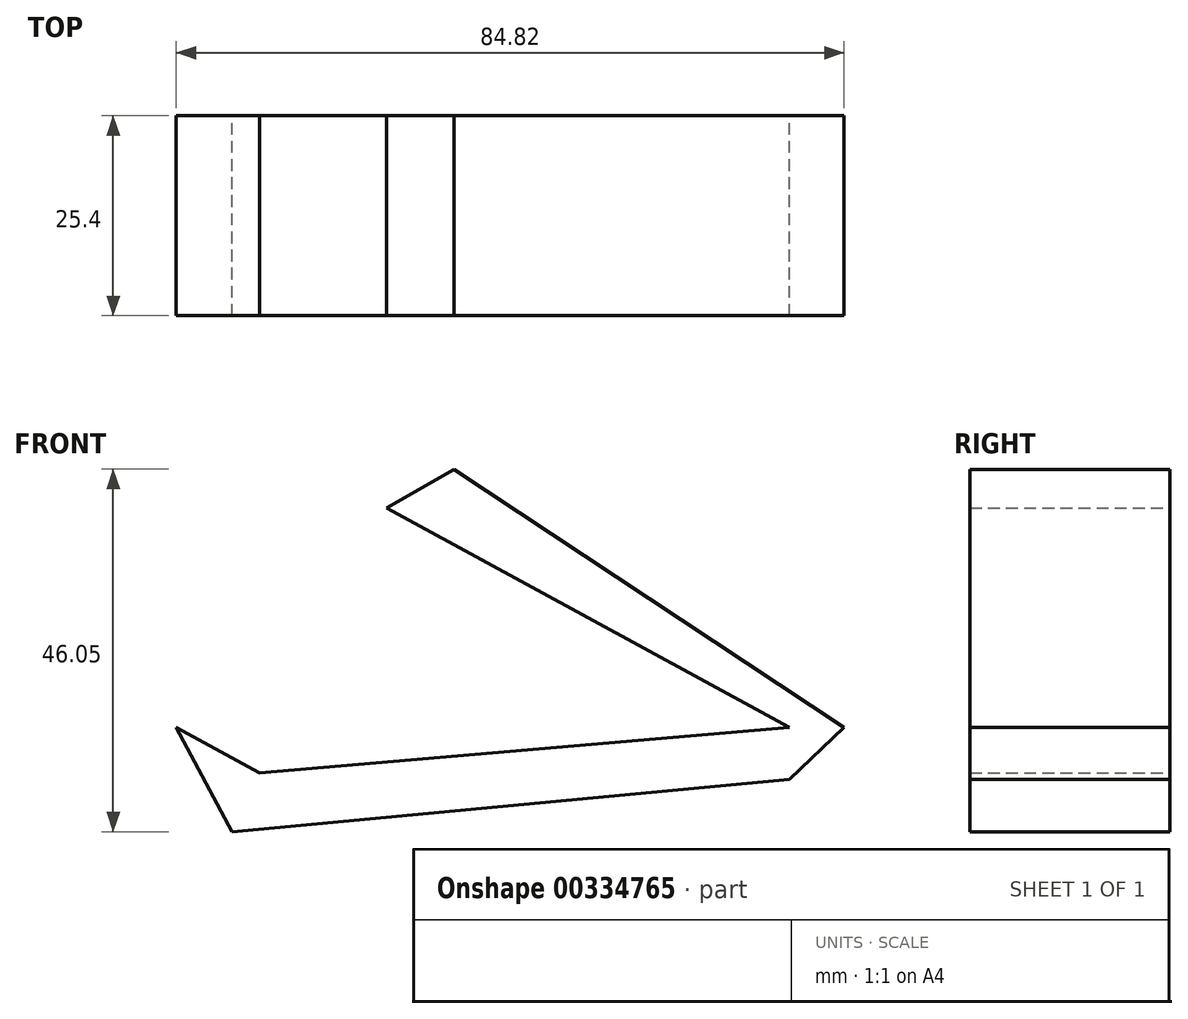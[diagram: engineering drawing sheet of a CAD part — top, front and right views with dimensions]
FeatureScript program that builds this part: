
annotation { "Feature Type Name" : "Feature", "Feature Type Description" : "" }
export const myFeature = defineFeature(function(context is Context, id is Id, definition is map)
    precondition{}
    {
        {
            var Q0;
            Q0=qCreatedBy(makeId("Front.planeOp"),FACE);
            var sketch = newSketch(context, id + "F0", { "sketchPlane" : qUnion([Q0])});
            skLineSegment(sketch, "E0", {"start": v(-51.23, 49.21) * mm, "end": v(0, 21.3) * mm});
            skLineSegment(sketch, "E1", {"start": v(0, 21.3) * mm, "end": v(-67.35, 15.54) * mm});
            skLineSegment(sketch, "E2", {"start": v(-67.35, 15.54) * mm, "end": v(-77.9, 21.3) * mm});
            skLineSegment(sketch, "E3", {"start": v(-77.9, 21.3) * mm, "end": v(-70.8, 8.06) * mm});
            skLineSegment(sketch, "E4", {"start": v(-70.8, 8.06) * mm, "end": v(0, 14.68) * mm});
            skLineSegment(sketch, "E5", {"start": v(0, 14.68) * mm, "end": v(6.9, 21.3) * mm});
            skLineSegment(sketch, "E6", {"start": v(6.9, 21.3) * mm, "end": v(-42.6, 54.1) * mm});
            skLineSegment(sketch, "E7", {"start": v(-42.6, 54.1) * mm, "end": v(-51.23, 49.21) * mm});
            skSolve(sketch);
        }
        {
            var Q0;
            Q0=makeQuery(id+"F0.imprint","IMPRINT",FACE,{"disambiguationData":[TD([[makeQuery(id+"F0.imprint","IMPRINT",EDGE,{"derivedFrom":sQuery(id+"F0.wireOp",EDGE,"E0")}),1.0]])]});
            extrude(context, id + "F1", {"entities" : qUnion([Q0]), "depth" : 25.4 * mm});
        }
    });
